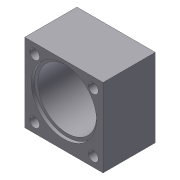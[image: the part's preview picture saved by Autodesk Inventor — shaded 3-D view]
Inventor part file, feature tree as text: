
AUTODESK INVENTOR PART (.ipt)
format: ipt  version: 2012 (Build 160160000, 160)  size: 121,856 bytes
history: native  units: in
note: dims shown in document units (in); Inventor stores cm internally (conversion verified against a paired STEP export)
features: sketch x3, extrude x3
ambient origin geometry x8: Origin, YZ Plane, XZ Plane, XY Plane, X Axis, Y Axis, Z Axis, Center Point
bodies: Solid1 (feature_tree)
feature tree (6):
  sketch  "Sketch1"  dims[d2=1.5in d4=1.5in]
  extrude  "Extrusion4"  Depth=1.5in
  extrude  "Extrusion5"  Depth=0.1875in
  extrude  "Extrusion6"  Depth=0.1875in
  sketch  "Sketch4"  dims[d5=0.192in d6=0.1875in]
  sketch  "Sketch5"  dims[d7=0.1875in d8=0.1875in d9=0.1875in d10=0.1875in d11=0.1875in d12=0.1875in d13=0.1875in d22=0.75in d23=0.25in d24=1.0in d25=0.0in d26=0.0625in d27=0.0625in d28=0.0in d29=0.0625in d30=0.0625in d31=0.0in]
